# Revit family: Electronics_Vocia_Biamp_Amplifier_VA-4030
name_source: partatom
category: Communication Devices
units: mm (PartAtom-declared; Revit-internal decimal feet)

## family parameters
Cut with Voids When Loaded = No
Host = Face
Maintain Annotation Orientation = No
OmniClass Number = 23.85.10.11.14.14.17
OmniClass Title = Sound Amplifiers
Part Type = Normal
Room Calculation Point = No
Round Connector Dimension = Use Diameter
Shared = No

## types (1)
- VA-4030
    100Hz-10kHz = < 0.3%
    50Hz-100Hz = < 0.5%
    Altitude = 0-10,000 Feet (0-3000 Meters) MSL
    Apparent Load = 120 VA
    Connector Description = 100-240 VAC, 50/60 Hz
    Default Elevation = 1219 mm
    Depth = 361 mm
    Description = Vocia® VA-4030 Amplifier
    Frequency Response (40Hz - 20kHz) = ± 2dB
    Height = 83 mm
    Housing Material = Biamp - Metal - Gray
    Humidity = 0 – 95% non-condensing
    Inputs = 20 bits, 48 kHz, 5-1/3 ms (fxed)
    Manufacturer = Biamp
    Max Power Consumption = 120 W
    Memory = 5.625 MB
    Model = VA-4030
    Network Connection = RJ-45 with shielded Ethernet (CAT5, CAT5e, CAT6 or CAT7)
    Number of Poles = 1
    Power Factor = 1
    Product Documentation Link = https://downloads.biamp.com
    Product Page URL = https://www.biamp.com
    Product data url = https://bimobject.com
    Signal to Noise Ratio = > 88 dB, unweighted
    Temperature Range = 23-104° F (-5 – 40° C)
    Total Output Power = 4 x 30W RMS, 120W maximum
    URL = https://www.biamp.com
    Version = 1
    Voltage = 240 V
    Weight = 26.00 lb
    Width = 483 mm

## geometry (parser evidence)
native form markers: Sweep x2
no freeform markers — native parametric forms only
